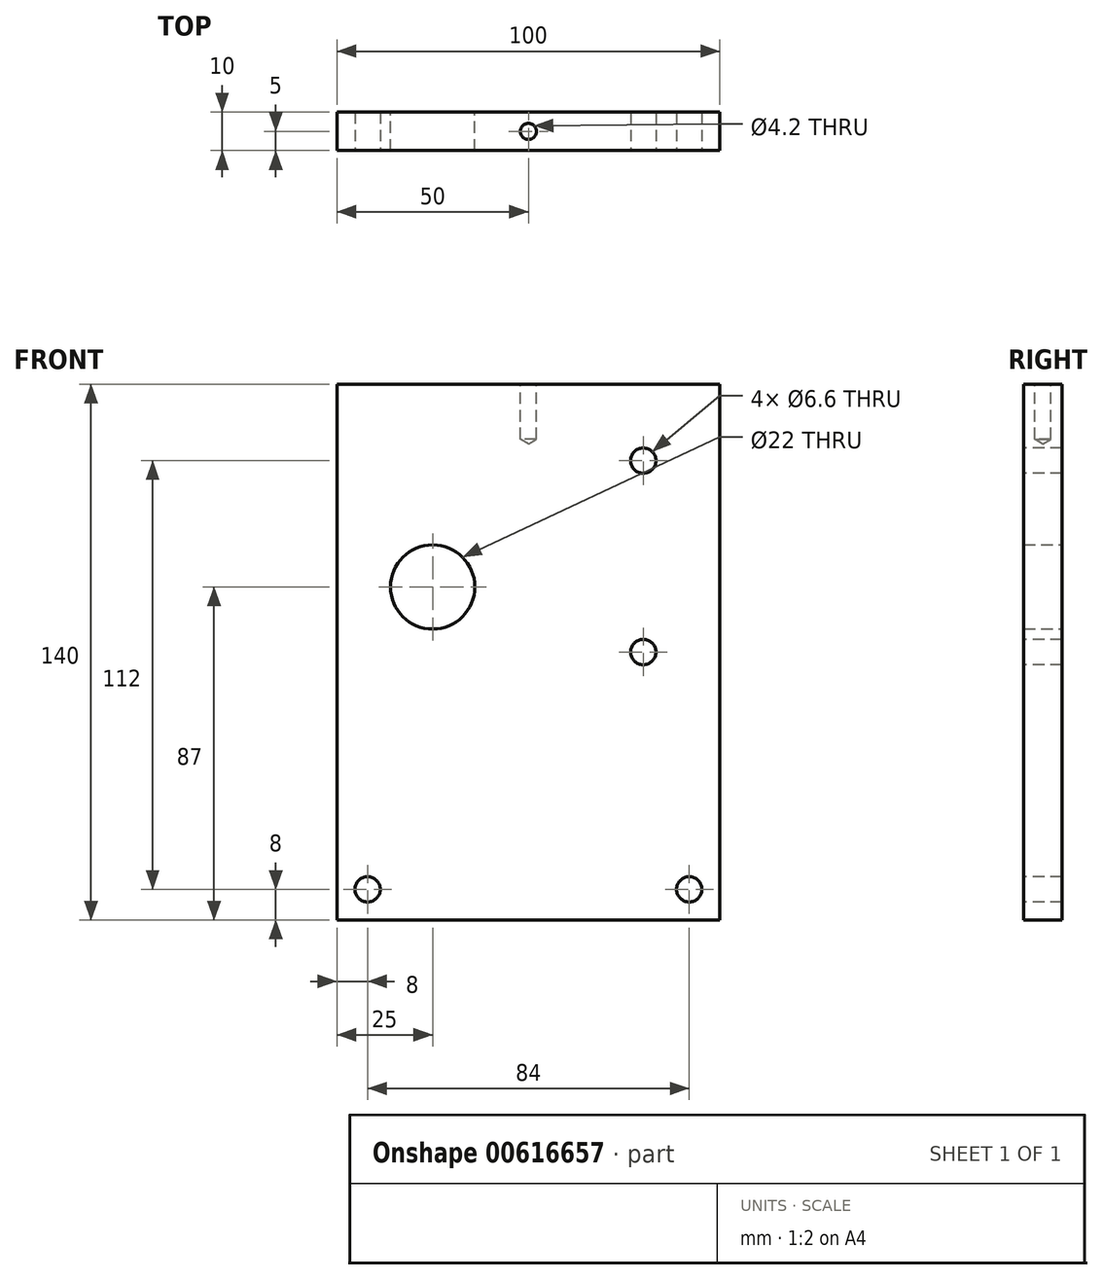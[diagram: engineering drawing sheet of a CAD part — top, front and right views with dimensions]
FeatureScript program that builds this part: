
annotation { "Feature Type Name" : "Feature", "Feature Type Description" : "" }
export const myFeature = defineFeature(function(context is Context, id is Id, definition is map)
    precondition{}
    {
        {
            var Q0;
            Q0=qCreatedBy(makeId("Front.planeOp"),FACE);
            var sketch = newSketch(context, id + "F0", { "sketchPlane" : qUnion([Q0])});
            skLineSegment(sketch, "E0.bottom", {"start": v(-50, 70) * mm, "end": v(50, 70) * mm});
            skLineSegment(sketch, "E0.top", {"start": v(-50, -70) * mm, "end": v(50, -70) * mm});
            skLineSegment(sketch, "E0.left", {"start": v(-50, 70) * mm, "end": v(-50, -70) * mm});
            skLineSegment(sketch, "E0.right", {"start": v(50, 70) * mm, "end": v(50, -70) * mm});
            skCircle(sketch, "E1", {"center": v(-25, 17) * mm, "radius": 11 * mm});
            skSolve(sketch);
        }
        {
            var Q0;
            Q0=makeQuery(id+"F0.imprint","IMPRINT",FACE,{"disambiguationData":[TD([[makeQuery(id+"F0.imprint","IMPRINT",EDGE,{"derivedFrom":sQuery(id+"F0.wireOp",EDGE,"E0.bottom")}),-1.0]])]});
            extrude(context, id + "F1", {"entities" : qUnion([Q0]), "depth" : 10 * mm, "offsetDistance" : 25 * mm});
        }
        {
            var Q0;
            Q0=makeQuery(id+"F1.opExtrude","CAP_FACE",FACE,{"disambiguationData":[OSD([sQuery(id+"F0.wireOp",EDGE,"E0.bottom"),sQuery(id+"F0.wireOp",EDGE,"E0.top"),sQuery(id+"F0.wireOp",EDGE,"E0.left"),sQuery(id+"F0.wireOp",EDGE,"E0.right"),sQuery(id+"F0.wireOp",EDGE,"E1")])],"isStart":false});
            var sketch = newSketch(context, id + "F2", { "sketchPlane" : qUnion([Q0])});
            skPoint(sketch, "E2", {"position": v(30, 50) * mm});
            skPoint(sketch, "E3", {"position": v(30, 0) * mm});
            skPoint(sketch, "E4", {"position": v(-42, -62) * mm});
            skPoint(sketch, "E5", {"position": v(42, -62) * mm});
            skSolve(sketch);
        }
        {
            var Q0;
            Q0=makeQuery(id+"F1.opExtrude","SWEPT_FACE",FACE,{"disambiguationData":[OSD([sQuery(id+"F0.wireOp",EDGE,"E0.bottom")])]});
            var sketch = newSketch(context, id + "F3", { "sketchPlane" : qUnion([Q0])});
            skPoint(sketch, "E6", {"position": v(0, -5) * mm});
            skSolve(sketch);
        }
        {
            var Q0;
            Q0=sQuery(id+"F3.wireOp",VERTEX,"E6");
            var Q1;
            Q1=makeQuery(id+"F1.opExtrude","SWEPT_BODY",BODY,{"disambiguationData":[OSD([sQuery(id+"F0.wireOp",EDGE,"E0.bottom"),sQuery(id+"F0.wireOp",EDGE,"E0.top"),sQuery(id+"F0.wireOp",EDGE,"E0.left"),sQuery(id+"F0.wireOp",EDGE,"E0.right"),sQuery(id+"F0.wireOp",EDGE,"E1")])]});
            hole(context, id + "F4", {"style" : HoleStyle.SIMPLE, "endStyle" : HoleEndStyle.BLIND, "standardTappedOrClearance" : lookupTablePath({ "standard" : "ISO", "engagement" : "75%", "pitch" : "0.8 mm", "size" : "M5", "type" : "Tapped" }), "standardBlindInLast" : lookupTablePath({ "standard" : "ISO", "engagement" : "75%", "pitch" : "0.8 mm", "size" : "M5", "type" : "Tapped" }), "holeDiameter" : 4.2 * mm, "majorDiameter" : 5 * mm, "showTappedDepth" : true, "holeDepth" : 14.4 * mm, "isTappedThrough" : true, "tappedDepth" : 12 * mm, "tapClearance" : 3, "locations" : qUnion([Q0]), "scope" : qUnion([Q1])});
        }
        {
            var Q0;
            Q0=sQuery(id+"F2.wireOp",VERTEX,"E2");
            var Q1;
            Q1=sQuery(id+"F2.wireOp",VERTEX,"E3");
            var Q2;
            Q2=sQuery(id+"F2.wireOp",VERTEX,"E4");
            var Q3;
            Q3=sQuery(id+"F2.wireOp",VERTEX,"E5");
            var Q4;
            Q4=makeQuery(id+"F1.opExtrude","SWEPT_BODY",BODY,{"disambiguationData":[OSD([sQuery(id+"F0.wireOp",EDGE,"E0.bottom"),sQuery(id+"F0.wireOp",EDGE,"E0.top"),sQuery(id+"F0.wireOp",EDGE,"E0.left"),sQuery(id+"F0.wireOp",EDGE,"E0.right"),sQuery(id+"F0.wireOp",EDGE,"E1")])]});
            hole(context, id + "F5", {"style" : HoleStyle.SIMPLE, "endStyle" : HoleEndStyle.THROUGH, "standardTappedOrClearance" : lookupTablePath({ "standard" : "ISO", "fit" : "Normal", "size" : "M6", "type" : "Clearance" }), "standardBlindInLast" : lookupTablePath({ "fit" : "Standard", "standard" : "ISO", "size" : "M6", "type" : "Clearance" }), "holeDiameter" : 6.6 * mm, "majorDiameter" : 6 * mm, "isTappedThrough" : true, "tappedDepth" : 12 * mm, "tapClearance" : 3, "locations" : qUnion([Q0, Q1, Q2, Q3]), "scope" : qUnion([Q4])});
        }
    });
